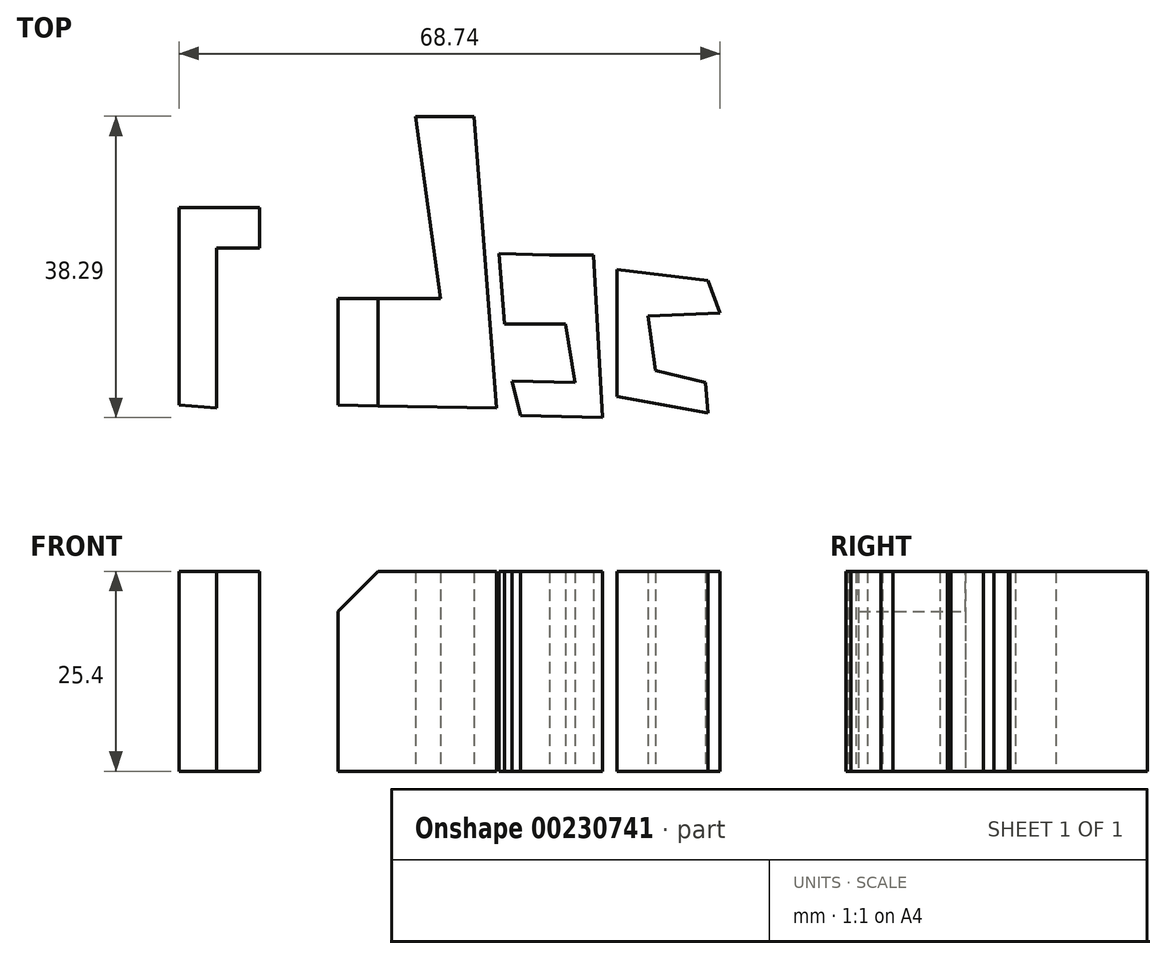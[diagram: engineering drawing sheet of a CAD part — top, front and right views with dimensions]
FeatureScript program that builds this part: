
annotation { "Feature Type Name" : "Feature", "Feature Type Description" : "" }
export const myFeature = defineFeature(function(context is Context, id is Id, definition is map)
    precondition{}
    {
        {
            var Q0;
            Q0=qCreatedBy(makeId("Top.planeOp"),FACE);
            var sketch = newSketch(context, id + "F0", { "sketchPlane" : qUnion([Q0])});
            skLineSegment(sketch, "E0", {"start": v(-90.36, 40.37) * mm, "end": v(-90.36, -5.98) * mm});
            skLineSegment(sketch, "E1", {"start": v(-90.36, -5.98) * mm, "end": v(-70.54, 0) * mm});
            skLineSegment(sketch, "E2", {"start": v(-70.54, 0) * mm, "end": v(-81.9, 16.47) * mm});
            skLineSegment(sketch, "E3", {"start": v(-81.9, 16.47) * mm, "end": v(-72.57, 37.1) * mm});
            skLineSegment(sketch, "E4", {"start": v(-72.57, 37.1) * mm, "end": v(-90.36, 40.37) * mm});
            skLineSegment(sketch, "E5", {"start": v(-69.11, 20.7) * mm, "end": v(-69.11, -4.39) * mm});
            skLineSegment(sketch, "E6", {"start": v(-69.11, 20.7) * mm, "end": v(-58.83, 20.7) * mm});
            skLineSegment(sketch, "E7", {"start": v(-58.83, 20.7) * mm, "end": v(-58.83, 15.56) * mm});
            skLineSegment(sketch, "E8", {"start": v(-58.83, 15.56) * mm, "end": v(-64.32, 15.56) * mm});
            skLineSegment(sketch, "E9", {"start": v(-64.32, 15.56) * mm, "end": v(-64.32, -4.74) * mm});
            skLineSegment(sketch, "E10", {"start": v(-64.32, -4.74) * mm, "end": v(-69.11, -4.39) * mm});
            skLineSegment(sketch, "E11", {"start": v(-54.75, 20.7) * mm, "end": v(-54.75, -4.39) * mm});
            skLineSegment(sketch, "E12", {"start": v(-54.75, -4.39) * mm, "end": v(-51.74, -4.39) * mm});
            skLineSegment(sketch, "E13", {"start": v(-51.74, -4.3) * mm, "end": v(-51.74, 20.7) * mm});
            skLineSegment(sketch, "E14", {"start": v(-51.74, 20.7) * mm, "end": v(-54.75, 20.7) * mm});
            skLineSegment(sketch, "E15", {"start": v(-41.1, 9.18) * mm, "end": v(-48.9, 9.18) * mm});
            skLineSegment(sketch, "E16", {"start": v(-48.9, 9.18) * mm, "end": v(-48.9, -4.39) * mm});
            skLineSegment(sketch, "E17", {"start": v(-48.9, -4.39) * mm, "end": v(-28.78, -4.74) * mm});
            skLineSegment(sketch, "E18", {"start": v(-28.78, -4.74) * mm, "end": v(-31.62, 32.3) * mm});
            skLineSegment(sketch, "E19", {"start": v(-31.62, 32.3) * mm, "end": v(-39.06, 32.3) * mm});
            skLineSegment(sketch, "E20", {"start": v(-39.06, 32.3) * mm, "end": v(-35.87, 9.18) * mm});
            skLineSegment(sketch, "E21", {"start": v(-35.87, 9.18) * mm, "end": v(-41.1, 9.18) * mm});
            skLineSegment(sketch, "E22", {"start": v(-22.03, 14.7) * mm, "end": v(-28.42, 14.85) * mm});
            skLineSegment(sketch, "E23", {"start": v(-28.42, 14.85) * mm, "end": v(-27.74, 5.95) * mm});
            skLineSegment(sketch, "E24", {"start": v(-27.74, 5.95) * mm, "end": v(-20.01, 5.95) * mm});
            skLineSegment(sketch, "E25", {"start": v(-22.03, 14.7) * mm, "end": v(-16.45, 14.7) * mm});
            skLineSegment(sketch, "E26", {"start": v(-16.45, 14.7) * mm, "end": v(-15.32, -5.98) * mm});
            skLineSegment(sketch, "E27", {"start": v(-15.32, -5.98) * mm, "end": v(-25.68, -5.71) * mm});
            skLineSegment(sketch, "E28", {"start": v(-25.68, -5.71) * mm, "end": v(-26.8, -1.31) * mm});
            skLineSegment(sketch, "E29", {"start": v(-26.8, -1.31) * mm, "end": v(-18.8, -1.52) * mm});
            skLineSegment(sketch, "E30", {"start": v(-18.8, -1.52) * mm, "end": v(-20.01, 5.95) * mm});
            skLineSegment(sketch, "E31", {"start": v(-9.5, 6.93) * mm, "end": v(-0.37, 7.34) * mm});
            skLineSegment(sketch, "E32", {"start": v(-0.37, 7.34) * mm, "end": v(-1.9, 11.46) * mm});
            skLineSegment(sketch, "E33", {"start": v(-1.9, 11.46) * mm, "end": v(-13.46, 12.83) * mm});
            skLineSegment(sketch, "E34", {"start": v(-13.46, 12.83) * mm, "end": v(-13.46, -3.25) * mm});
            skLineSegment(sketch, "E35", {"start": v(-13.46, -3.25) * mm, "end": v(-1.9, -5.36) * mm});
            skLineSegment(sketch, "E36", {"start": v(-1.9, -5.36) * mm, "end": v(-2.2, -1.52) * mm});
            skLineSegment(sketch, "E37", {"start": v(-2.2, -1.52) * mm, "end": v(-8.53, 0) * mm});
            skLineSegment(sketch, "E38", {"start": v(-8.53, 0) * mm, "end": v(-9.5, 6.93) * mm});
            skSolve(sketch);
        }
        {
            var Q0;
            Q0=makeQuery(id+"F0.imprint","IMPRINT",FACE,{"disambiguationData":[TD([[makeQuery(id+"F0.imprint","IMPRINT",EDGE,{"derivedFrom":sQuery(id+"F0.wireOp",EDGE,"E5")}),1.0]])]});
            var Q1;
            Q1=makeQuery(id+"F0.imprint","IMPRINT",FACE,{"disambiguationData":[TD([[makeQuery(id+"F0.imprint","IMPRINT",EDGE,{"derivedFrom":sQuery(id+"F0.wireOp",EDGE,"E15")}),1.0]])]});
            var Q2;
            Q2=makeQuery(id+"F0.imprint","IMPRINT",FACE,{"disambiguationData":[TD([[makeQuery(id+"F0.imprint","IMPRINT",EDGE,{"derivedFrom":sQuery(id+"F0.wireOp",EDGE,"E22")}),1.0]])]});
            var Q3;
            Q3=makeQuery(id+"F0.imprint","IMPRINT",FACE,{"disambiguationData":[TD([[makeQuery(id+"F0.imprint","IMPRINT",EDGE,{"derivedFrom":sQuery(id+"F0.wireOp",EDGE,"E31")}),1.0]])]});
            extrude(context, id + "F1", {"entities" : qUnion([Q0, Q1, Q2, Q3]), "depth" : 25.4 * mm});
        }
        {
            var Q0;
            Q0=makeQuery(id+"F1.opExtrude","CAP_EDGE",EDGE,{"disambiguationData":[OSD([sQuery(id+"F0.wireOp",EDGE,"E16")])],"isStart":false});
            chamfer(context, id + "F2", {"entities" : qUnion([Q0]), "width" : 5.08 * mm, "tangentPropagation" : true});
        }
    });
